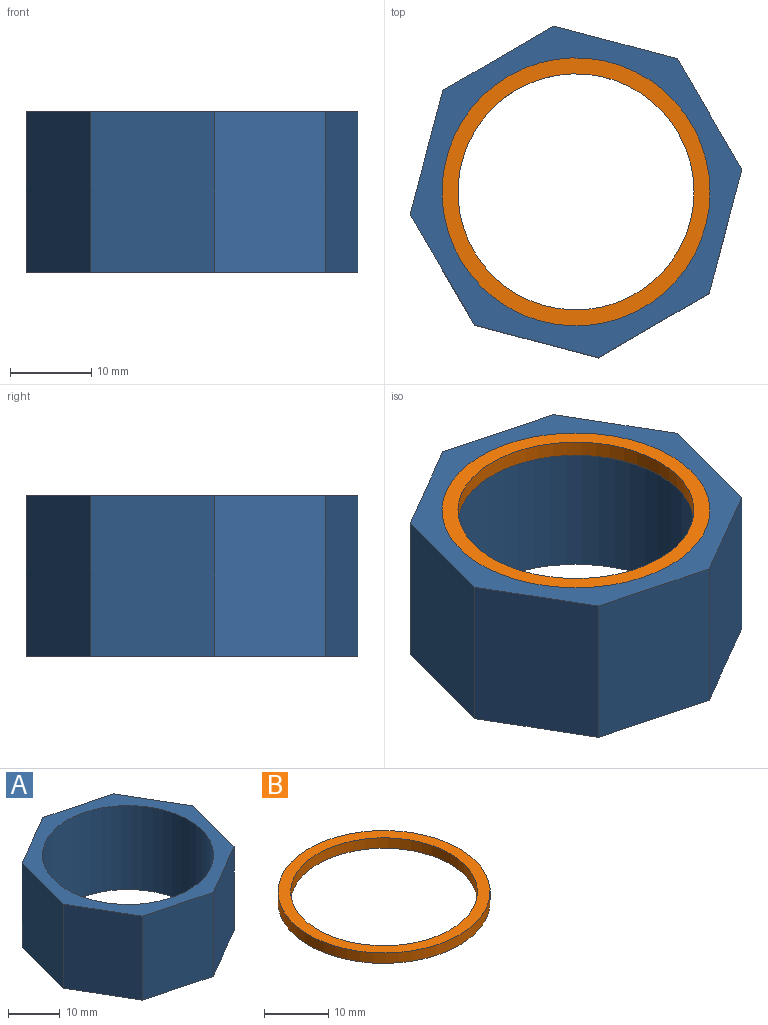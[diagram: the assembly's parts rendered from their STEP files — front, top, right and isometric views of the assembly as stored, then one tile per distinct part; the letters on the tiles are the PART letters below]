
ASSEMBLY  parts=2 mates=1
PART A: 11 faces, bbox 40.9x40.9x19.8 mm
  f0: plane 19.81x13.64mm, normal (0.86,0.5,0), area 312.7mm2, adj f1,f7,f8,f9
  f1: plane 19.81x15.26mm, normal (0.25,0.97,0), area 312.7mm2, adj f0,f2,f8,f9
  f2: plane 19.81x13.64mm, normal (-0.5,0.86,0), area 312.7mm2, adj f1,f3,f8,f9
  f3: plane 19.81x15.26mm, normal (-0.97,0.25,0), area 312.7mm2, adj f2,f4,f8,f9
  f4: plane 19.81x13.64mm, normal (-0.86,-0.5,0), area 312.7mm2, adj f3,f5,f8,f9
  f5: plane 19.81x15.26mm, normal (-0.25,-0.97,0), area 312.7mm2, adj f4,f6,f8,f9
  f6: plane 19.81x13.64mm, normal (0.5,-0.86,0), area 312.7mm2, adj f5,f7,f8,f9
  f7: plane 19.81x15.26mm, normal (0.97,-0.25,0), area 312.7mm2, adj f0,f6,f8,f9
  f8: plane 40.86x40.86mm, normal (0,0,1), area 346.2mm2, adj f0,f1,f2,f3,f4,f5,f6,f7
  f9: plane 40.86x40.86mm, normal (0,0,-1), area 346.2mm2, adj f0,f1,f2,f3,f4,f5,f6,f7
  f10: cylinder r=16.51mm len=33.02mm, axis (0,0,1), area 2055.2mm2, adj f8,f9
PART B: 4 faces, bbox 33x33x2 mm
  f0: cylinder r=14.54mm len=29.08mm, axis (0,0,-1), area 181mm2, adj f2,f3
  f1: cylinder r=16.51mm len=33.02mm, axis (0,0,-1), area 205.5mm2, adj f2,f3
  f2: plane 33.02x33.02mm, normal (0,0,1), area 192mm2, adj f0,f1
  f3: plane 33.02x33.02mm, normal (0,0,-1), area 192mm2, adj f0,f1
PLACE A t=(-72.17,2.36,-18.7)mm
PLACE B t=(-72.17,2.36,-0.87)mm
MATE fastened A.f10 <-> B.f0  axis (0,0,1) through (-72.17,2.36,1.11)mm
